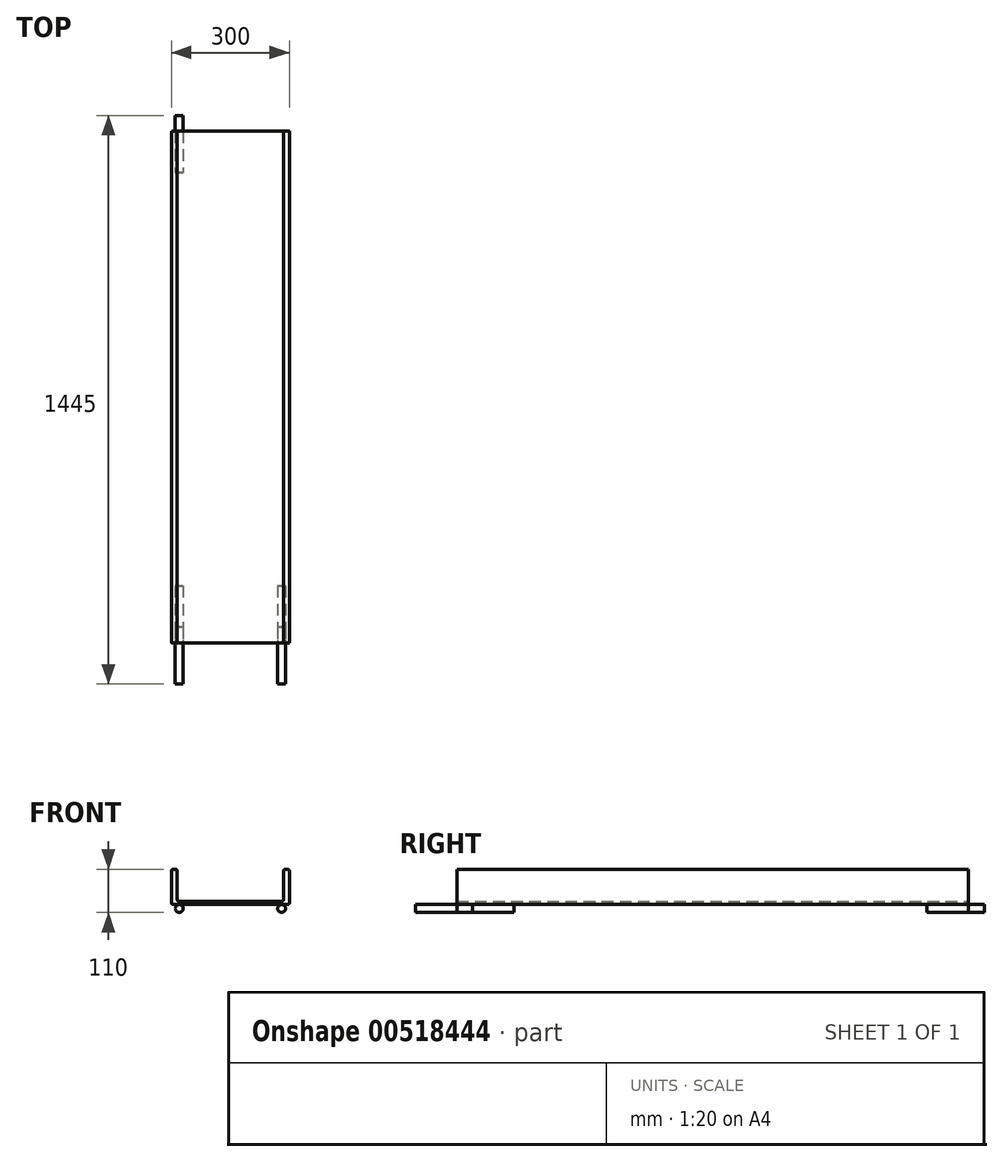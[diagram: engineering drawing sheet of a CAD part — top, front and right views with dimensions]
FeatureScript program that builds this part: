
annotation { "Feature Type Name" : "Feature", "Feature Type Description" : "" }
export const myFeature = defineFeature(function(context is Context, id is Id, definition is map)
    precondition{}
    {
        {
            var Q0;
            Q0=qCreatedBy(makeId("Front.planeOp"),FACE);
            var sketch = newSketch(context, id + "F0", { "sketchPlane" : qUnion([Q0])});
            skLineSegment(sketch, "E0", {"start": v(0, 5) * mm, "end": v(0, 85) * mm});
            skLineSegment(sketch, "E1", {"start": v(5, 90) * mm, "end": v(10, 90) * mm});
            skLineSegment(sketch, "E2", {"start": v(15, 85) * mm, "end": v(15, 13) * mm});
            skLineSegment(sketch, "E3", {"start": v(20, 8) * mm, "end": v(280, 8) * mm});
            skLineSegment(sketch, "E4", {"start": v(285, 13) * mm, "end": v(285, 85) * mm});
            skLineSegment(sketch, "E5", {"start": v(290, 90) * mm, "end": v(295, 90) * mm});
            skLineSegment(sketch, "E6", {"start": v(300, 85) * mm, "end": v(300, 5) * mm});
            skLineSegment(sketch, "E7", {"start": v(295, 0) * mm, "end": v(5, 0) * mm});
            skPoint(sketch, "E8.visualSharp", {"position": v(15, 90) * mm});
            skArc(sketch, "E8.filletArc", {"start": v(15, 85) * mm, "mid": v(13.54, 88.54) * mm, "end": v(10, 90) * mm});
            skPoint(sketch, "E9.visualSharp", {"position": v(0, 90) * mm});
            skArc(sketch, "E9.filletArc", {"start": v(5, 90) * mm, "mid": v(1.46, 88.54) * mm, "end": v(0, 85) * mm});
            skPoint(sketch, "E10.visualSharp", {"position": v(0, 0) * mm});
            skArc(sketch, "E10.filletArc", {"start": v(0, 5) * mm, "mid": v(1.46, 1.46) * mm, "end": v(5, 0) * mm});
            skPoint(sketch, "E11.visualSharp", {"position": v(15, 8) * mm});
            skArc(sketch, "E11.filletArc", {"start": v(15, 13) * mm, "mid": v(16.46, 9.46) * mm, "end": v(20, 8) * mm});
            skPoint(sketch, "E12.visualSharp", {"position": v(285, 8) * mm});
            skArc(sketch, "E12.filletArc", {"start": v(280, 8) * mm, "mid": v(283.54, 9.46) * mm, "end": v(285, 13) * mm});
            skPoint(sketch, "E13.visualSharp", {"position": v(285, 90) * mm});
            skArc(sketch, "E13.filletArc", {"start": v(290, 90) * mm, "mid": v(286.46, 88.54) * mm, "end": v(285, 85) * mm});
            skPoint(sketch, "E14.visualSharp", {"position": v(300, 90) * mm});
            skArc(sketch, "E14.filletArc", {"start": v(300, 85) * mm, "mid": v(298.54, 88.54) * mm, "end": v(295, 90) * mm});
            skPoint(sketch, "E15.visualSharp", {"position": v(300, 0) * mm});
            skArc(sketch, "E15.filletArc", {"start": v(295, 0) * mm, "mid": v(298.54, 1.46) * mm, "end": v(300, 5) * mm});
            skLineSegment(sketch, "E16", {"start": v(150, 109.34) * mm, "end": v(150, -48.1) * mm, "construction": true});
            skCircle(sketch, "E17", {"center": v(20, -10) * mm, "radius": 10 * mm});
            skCircle(sketch, "E18.MirrorC", {"center": v(280, -10) * mm, "radius": 10 * mm});
            skLineSegment(sketch, "E19.MirrorCS", {"start": v(5, 0) * mm, "end": v(295, 0) * mm});
            skLineSegment(sketch, "E20.MirrorCS", {"start": v(280, 8) * mm, "end": v(20, 8) * mm});
            skLineSegment(sketch, "E21.MirrorCS", {"start": v(300, 5) * mm, "end": v(300, 85) * mm});
            skSolve(sketch);
        }
        {
            var Q0;
            Q0=makeQuery(id+"F0.imprint","IMPRINT",FACE,{"disambiguationData":[TD([[makeQuery(id+"F0.imprint","IMPRINT",EDGE,{"derivedFrom":sQuery(id+"F0.wireOp",EDGE,"E0")}),-1.0]])]});
            extrude(context, id + "F1", {"entities" : qUnion([Q0]), "depth" : 1300 * mm, "offsetDistance" : 25 * mm});
        }
        {
            var Q0;
            Q0=makeQuery(id+"F0.imprint","IMPRINT",FACE,{"disambiguationData":[TD([[makeQuery(id+"F0.imprint","IMPRINT",EDGE,{"derivedFrom":sQuery(id+"F0.wireOp",EDGE,"E17")}),1.0]])]});
            var Q1;
            Q1=makeQuery(id+"F0.imprint","IMPRINT",FACE,{"disambiguationData":[TD([[makeQuery(id+"F0.imprint","IMPRINT",EDGE,{"derivedFrom":sQuery(id+"F0.wireOp",EDGE,"E18.MirrorC")}),-1.0]])]});
            extrude(context, id + "F2", {"entities" : qUnion([Q0, Q1]), "operationType" : NewBodyOperationType.ADD, "depth" : 105 * mm, "offsetDistance" : 25 * mm});
        }
        {
            var Q0;
            Q0=makeQuery(id+"F2.opExtrude","CAP_FACE",FACE,{"disambiguationData":[OSD([sQuery(id+"F0.wireOp",EDGE,"E17")])],"isStart":false});
            var Q1;
            Q1=makeQuery(id+"F2.opExtrude","CAP_FACE",FACE,{"disambiguationData":[OSD([sQuery(id+"F0.wireOp",EDGE,"E18.MirrorC")])],"isStart":false});
            extrude(context, id + "F3", {"entities" : qUnion([Q0, Q1]), "oppositeDirection" : true, "depth" : 145 * mm, "offsetDistance" : 25 * mm});
        }
        {
            var Q0;
            Q0=makeQuery(id+"F1.opExtrude","CAP_FACE",FACE,{"disambiguationData":[OSD([sQuery(id+"F0.wireOp",EDGE,"E0"),sQuery(id+"F0.wireOp",EDGE,"E1"),sQuery(id+"F0.wireOp",EDGE,"E2"),sQuery(id+"F0.wireOp",EDGE,"E4"),sQuery(id+"F0.wireOp",EDGE,"E5"),sQuery(id+"F0.wireOp",EDGE,"E8.filletArc"),sQuery(id+"F0.wireOp",EDGE,"E9.filletArc"),sQuery(id+"F0.wireOp",EDGE,"E10.filletArc"),sQuery(id+"F0.wireOp",EDGE,"E11.filletArc"),sQuery(id+"F0.wireOp",EDGE,"E12.filletArc"),sQuery(id+"F0.wireOp",EDGE,"E13.filletArc"),sQuery(id+"F0.wireOp",EDGE,"E14.filletArc"),sQuery(id+"F0.wireOp",EDGE,"E15.filletArc"),sQuery(id+"F0.wireOp",EDGE,"E19.MirrorCS"),sQuery(id+"F0.wireOp",EDGE,"E20.MirrorCS"),sQuery(id+"F0.wireOp",EDGE,"E21.MirrorCS")])],"isStart":false});
            var sketch = newSketch(context, id + "F4", { "sketchPlane" : qUnion([Q0])});
            skCircle(sketch, "E22", {"center": v(20, -10) * mm, "radius": 10 * mm});
            skCircle(sketch, "E23", {"center": v(280, -10) * mm, "radius": 10 * mm});
            skSolve(sketch);
        }
        {
            var Q0;
            Q0=makeQuery(id+"F4.imprint","IMPRINT",FACE,{"disambiguationData":[TD([[makeQuery(id+"F4.imprint","IMPRINT",EDGE,{"derivedFrom":sQuery(id+"F4.wireOp",EDGE,"E22")}),1.0]])]});
            var Q1;
            Q1=makeQuery(id+"F4.imprint","IMPRINT",FACE,{"disambiguationData":[TD([[makeQuery(id+"F4.imprint","IMPRINT",EDGE,{"derivedFrom":sQuery(id+"F4.wireOp",EDGE,"E23")}),1.0]])]});
            extrude(context, id + "F5", {"entities" : qUnion([Q0, Q1]), "depth" : 105 * mm, "offsetDistance" : 25 * mm});
        }
        {
            var Q0;
            Q0 = qSketchRegion(id + "F4", true);
            var Q1;
            Q1=makeQuery(id+"F5.opExtrude","CAP_FACE",FACE,{"disambiguationData":[OSD([sQuery(id+"F4.wireOp",EDGE,"E22")])],"isStart":false});
            var Q2;
            Q2=makeQuery(id+"F5.opExtrude","CAP_FACE",FACE,{"disambiguationData":[OSD([sQuery(id+"F4.wireOp",EDGE,"E23")])],"isStart":false});
            extrude(context, id + "F6", {"entities" : qUnion([Q0, Q1, Q2]), "oppositeDirection" : true, "depth" : 145 * mm, "offsetDistance" : 25 * mm});
        }
    });
